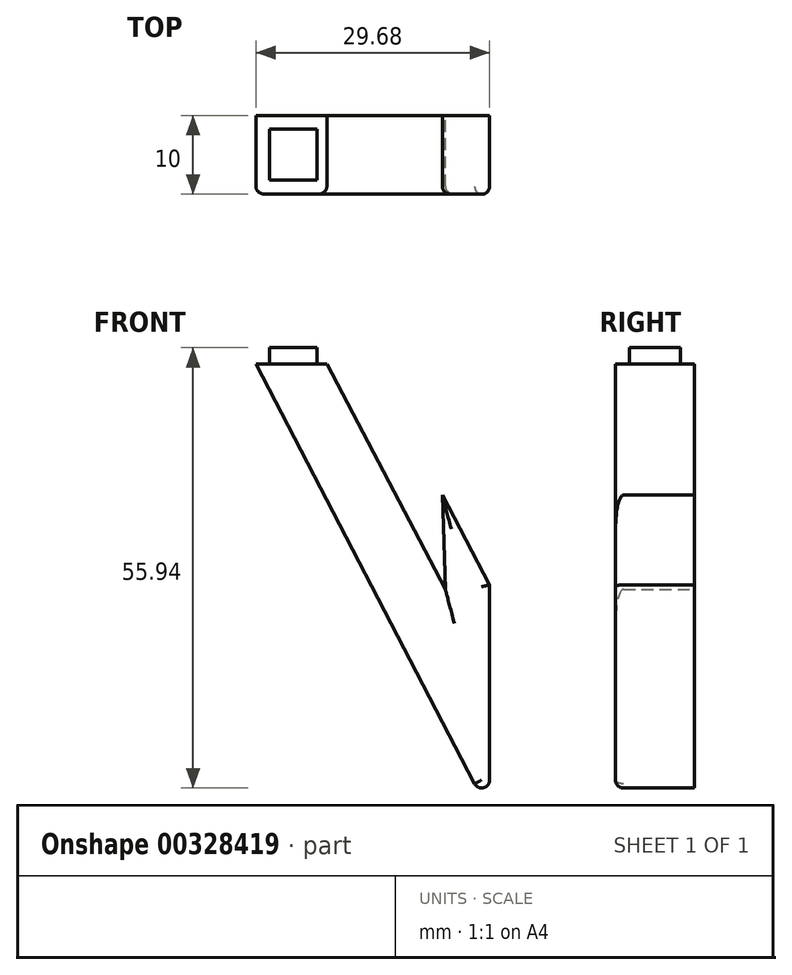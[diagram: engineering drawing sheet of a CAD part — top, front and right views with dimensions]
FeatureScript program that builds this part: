
annotation { "Feature Type Name" : "Feature", "Feature Type Description" : "" }
export const myFeature = defineFeature(function(context is Context, id is Id, definition is map)
    precondition{}
    {
        {
            var Q0;
            Q0=qCreatedBy(makeId("Front.planeOp"),FACE);
            var sketch = newSketch(context, id + "F0", { "sketchPlane" : qUnion([Q0])});
            skPoint(sketch, "E0", {"position": v(0, 0) * mm});
            skPoint(sketch, "E1", {"position": v(9, 0) * mm});
            skLineSegment(sketch, "E2", {"start": v(0, 0) * mm, "end": v(9, 0) * mm});
            skPoint(sketch, "E3", {"position": v(24.06, -28.6) * mm});
            skLineSegment(sketch, "E4", {"start": v(9, 0) * mm, "end": v(24.06, -28.6) * mm});
            skPoint(sketch, "E5", {"position": v(23.67, -16.6) * mm});
            skLineSegment(sketch, "E6", {"start": v(24.06, -28.6) * mm, "end": v(23.67, -16.6) * mm});
            skLineSegment(sketch, "E7", {"start": v(23.67, -16.6) * mm, "end": v(29.68, -28.02) * mm});
            skLineSegment(sketch, "E8", {"start": v(29.68, -28.02) * mm, "end": v(29.68, -56.92) * mm});
            skLineSegment(sketch, "E9", {"start": v(0, 0) * mm, "end": v(29.68, -56.92) * mm});
            skSolve(sketch);
        }
        {
            var Q0;
            Q0=makeQuery(id+"F0.imprint","IMPRINT",FACE,{"disambiguationData":[TD([[makeQuery(id+"F0.imprint","IMPRINT",EDGE,{"derivedFrom":sQuery(id+"F0.wireOp",EDGE,"E2")}),-1.0]])]});
            extrude(context, id + "F1", {"entities" : qUnion([Q0]), "depth" : 10 * mm});
        }
        {
            var Q0;
            Q0=makeQuery(id+"F1.opExtrude","SWEPT_FACE",FACE,{"disambiguationData":[OSD([sQuery(id+"F0.wireOp",EDGE,"E2")])]});
            var sketch = newSketch(context, id + "F2", { "sketchPlane" : qUnion([Q0])});
            skPoint(sketch, "E10", {"position": v(1.75, -1.75) * mm});
            skPoint(sketch, "E11", {"position": v(7.77, -1.75) * mm});
            skPoint(sketch, "E12", {"position": v(1.75, -8.23) * mm});
            skPoint(sketch, "E13", {"position": v(7.75, -8.23) * mm});
            skLineSegment(sketch, "E14", {"start": v(1.75, -1.75) * mm, "end": v(1.75, -8.23) * mm});
            skLineSegment(sketch, "E15", {"start": v(1.75, -8.23) * mm, "end": v(7.75, -8.23) * mm});
            skLineSegment(sketch, "E16", {"start": v(7.77, -1.75) * mm, "end": v(7.75, -8.23) * mm});
            skLineSegment(sketch, "E17", {"start": v(7.77, -1.75) * mm, "end": v(1.75, -1.75) * mm});
            skSolve(sketch);
        }
        {
            var Q0;
            Q0 = qSketchRegion(id + "F2", true);
            extrude(context, id + "F3", {"entities" : qUnion([Q0]), "operationType" : NewBodyOperationType.ADD, "depth" : 2.1 * mm});
        }
        {
            var Q0;
            Q0=makeQuery(id+"F1.opExtrude","CAP_EDGE",EDGE,{"disambiguationData":[OSD([sQuery(id+"F0.wireOp",EDGE,"E9")])],"isStart":false});
            fillet(context, id + "F4", {"entities" : qUnion([Q0]), "radius" : 1 * mm, "tangentPropagation" : true, "allowEdgeOverflow" : false});
        }
        {
            var Q0;
            Q0=makeQuery(id+"F1.opExtrude","CAP_EDGE",EDGE,{"disambiguationData":[OSD([sQuery(id+"F0.wireOp",EDGE,"E4")])],"isStart":false});
            var Q1;
            Q1=makeQuery(id+"F1.opExtrude","CAP_EDGE",EDGE,{"disambiguationData":[OSD([sQuery(id+"F0.wireOp",EDGE,"E6")])],"isStart":false});
            var Q2;
            Q2=makeQuery(id+"F1.opExtrude","CAP_EDGE",EDGE,{"disambiguationData":[OSD([sQuery(id+"F0.wireOp",EDGE,"E7")])],"isStart":false});
            var Q3;
            Q3=makeQuery(id+"F1.opExtrude","CAP_EDGE",EDGE,{"disambiguationData":[OSD([sQuery(id+"F0.wireOp",EDGE,"E8")])],"isStart":false});
            fillet(context, id + "F5", {"entities" : qUnion([Q0, Q1, Q2, Q3]), "radius" : 1 * mm, "tangentPropagation" : true, "allowEdgeOverflow" : false});
        }
    });
